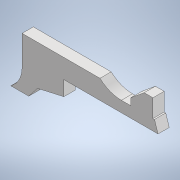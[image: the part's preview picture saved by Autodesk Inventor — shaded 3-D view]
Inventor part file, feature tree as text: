
AUTODESK INVENTOR PART (.ipt)
format: ipt  version: 2022 (Build 260153000, 153)  size: 757,248 bytes
history: native  units: in
note: dims shown in document units (in); Inventor stores cm internally (conversion verified against a paired STEP export)
features: other x5, sheet_metal_op x1, sketch x1, reference x1
ambient origin geometry x8: Origin, YZ Plane, XZ Plane, XY Plane, X Axis, Y Axis, Z Axis, Center Point
bodies: Solid1 (feature_tree)
feature tree (8):
  sheet_metal_op  "Face1"
  sketch  "Sketch1"  dims[d1=3.0666in d2=3.0666in d31=0.0591in]
  other  "Image1"
  reference  "Reference1"
  other  "Plate1"
  parser-record x1  (decoder bookkeeping rows leaked as tree rows — omitted from the tree; the rows remain in map.json)
  other  "Assembly1.iam"
  other  "sheetmettaal:2"
note: 1 file-system path scrubbed to <path> (originals preserved in map.json)
